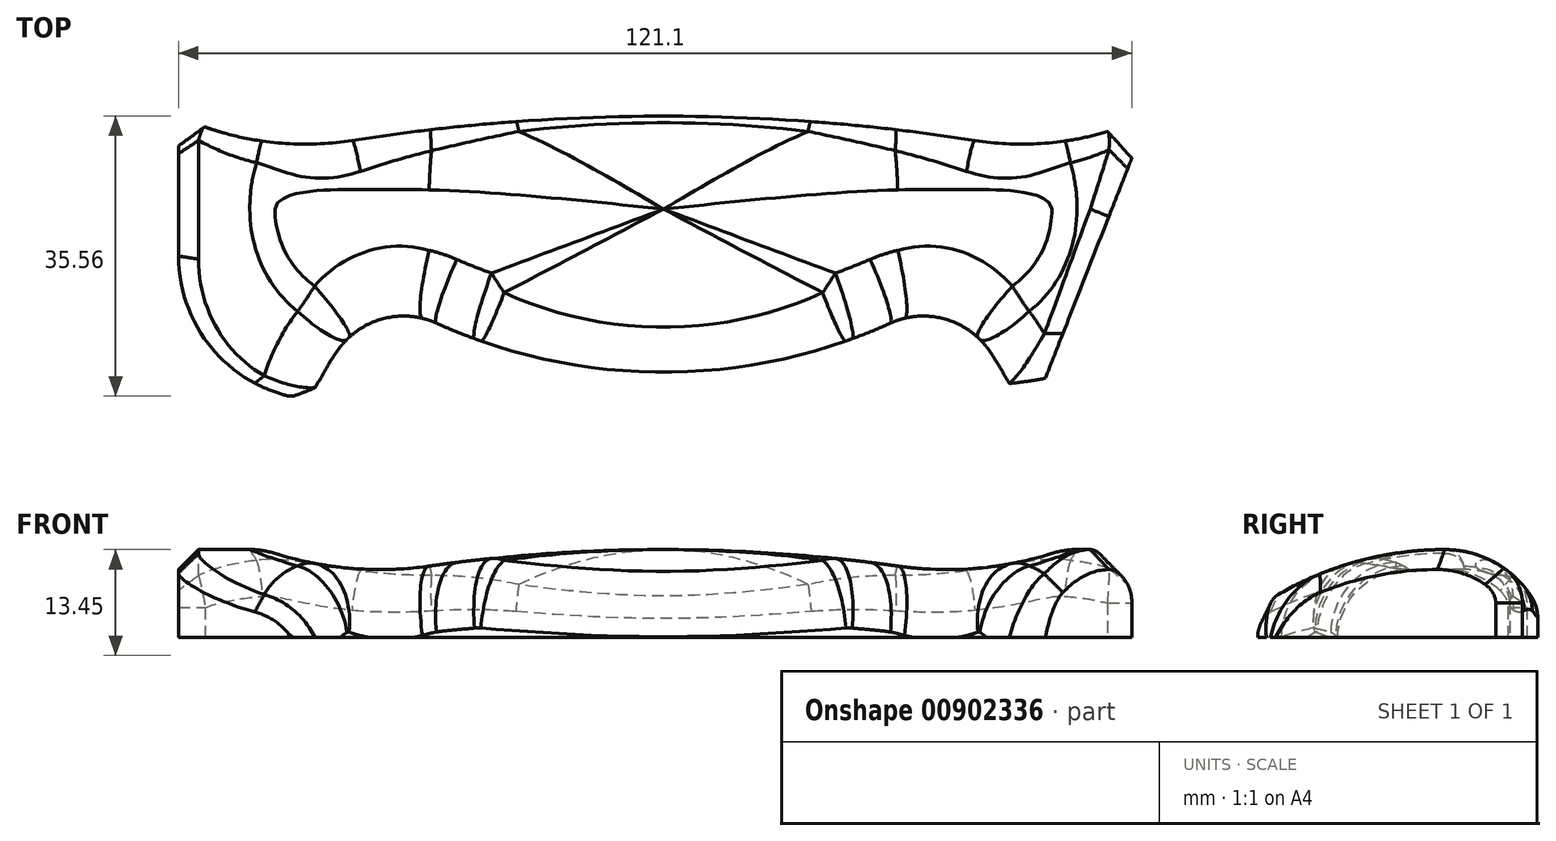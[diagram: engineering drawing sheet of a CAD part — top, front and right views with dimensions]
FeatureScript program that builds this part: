
annotation { "Feature Type Name" : "Feature", "Feature Type Description" : "" }
export const myFeature = defineFeature(function(context is Context, id is Id, definition is map)
    precondition{}
    {
        {
            var Q0;
            Q0=qCreatedBy(makeId("Top.planeOp"),FACE);
            var sketch = newSketch(context, id + "F0", { "sketchPlane" : qUnion([Q0])});
            skLineSegment(sketch, "E0", {"start": v(-61.6, 35.56) * mm, "end": v(-47.63, 0) * mm, "construction": true});
            skLineSegment(sketch, "E1", {"start": v(-47.62, 0) * mm, "end": v(47.62, 0) * mm, "construction": true});
            skLineSegment(sketch, "E2", {"start": v(47.63, 0) * mm, "end": v(61.6, 35.56) * mm, "construction": true});
            skLineSegment(sketch, "E3", {"start": v(61.6, 35.56) * mm, "end": v(-61.6, 35.56) * mm, "construction": true});
            skLineSegment(sketch, "E4", {"start": v(0, 0) * mm, "end": v(0, 35.56) * mm, "construction": true});
            skSolve(sketch);
        }
        {
            var Q0;
            Q0=qCreatedBy(makeId("Top.planeOp"),FACE);
            var sketch = newSketch(context, id + "F1", { "sketchPlane" : qUnion([Q0])});
            skLineSegment(sketch, "E5.0", {"start": v(61.6, 35.56) * mm, "end": v(-61.6, 35.56) * mm, "construction": true});
            skLineSegment(sketch, "E6.0", {"start": v(-61.6, 35.56) * mm, "end": v(-47.63, 0) * mm, "construction": true});
            skLineSegment(sketch, "E7.0", {"start": v(-47.62, 0) * mm, "end": v(47.62, 0) * mm, "construction": true});
            skLineSegment(sketch, "E8.0", {"start": v(47.63, 0) * mm, "end": v(61.6, 35.56) * mm, "construction": true});
            skArc(sketch, "E9", {"start": v(58.88, 28.64) * mm, "mid": v(49.26, 30.74) * mm, "end": v(39.57, 32.46) * mm, "construction": true});
            skArc(sketch, "E10", {"start": v(39.57, 32.46) * mm, "mid": v(50.81, 32.37) * mm, "end": v(61.6, 35.56) * mm});
            skArc(sketch, "E11", {"start": v(-28.83, 9.25) * mm, "mid": v(-38.53, 8.54) * mm, "end": v(-43.18, 0) * mm});
            skArc(sketch, "E12", {"start": v(-28.83, 9.25) * mm, "mid": v(0, 3.03) * mm, "end": v(28.83, 9.25) * mm});
            skArc(sketch, "E13", {"start": v(39.57, 32.46) * mm, "mid": v(0, 35.56) * mm, "end": v(-39.57, 32.46) * mm});
            skLineSegment(sketch, "E14", {"start": v(61.6, 35.56) * mm, "end": v(47.63, 0) * mm});
            skLineSegment(sketch, "E15", {"start": v(43.18, 0) * mm, "end": v(47.62, 0) * mm});
            skArc(sketch, "E16", {"start": v(43.18, 0) * mm, "mid": v(38.53, 8.54) * mm, "end": v(28.83, 9.25) * mm});
            skLineSegment(sketch, "E17", {"start": v(-47.63, 0) * mm, "end": v(-43.18, 0) * mm});
            skLineSegment(sketch, "E18", {"start": v(0, -218.44) * mm, "end": v(0, 72.88) * mm, "construction": true});
            skArc(sketch, "E19", {"start": v(-61.6, 35.56) * mm, "mid": v(-50.81, 32.37) * mm, "end": v(-39.57, 32.46) * mm});
            skArc(sketch, "E20", {"start": v(-39.57, 32.46) * mm, "mid": v(-49.26, 30.74) * mm, "end": v(-58.88, 28.64) * mm, "construction": true});
            skLineSegment(sketch, "E21", {"start": v(-61.6, 35.56) * mm, "end": v(-61.6, 17.78) * mm});
            skLineSegment(sketch, "E22", {"start": v(-61.6, 17.78) * mm, "end": v(-54.61, 17.78) * mm, "construction": true});
            skArc(sketch, "E23", {"start": v(-61.6, 17.78) * mm, "mid": v(-57.68, 6.47) * mm, "end": v(-47.63, 0) * mm});
            skSolve(sketch);
        }
        {
            var Q0;
            Q0=qSketchRegion(id+"F1",true);
            extrude(context, id + "F2", {"entities" : qUnion([Q0]), "depth" : 19.05 * mm, "offsetDistance" : 25.4 * mm});
        }
        {
            var Q0;
            Q0=qCreatedBy(makeId("Right.planeOp"),FACE);
            var sketch = newSketch(context, id + "F3", { "sketchPlane" : qUnion([Q0])});
            skLineSegment(sketch, "E24.0", {"start": v(35.56, 0) * mm, "end": v(0, 0) * mm, "construction": true});
            skLineSegment(sketch, "E25", {"start": v(35.56, 0) * mm, "end": v(35.56, 3.8) * mm, "construction": true});
            skLineSegment(sketch, "E26", {"start": v(35.56, 3.8) * mm, "end": v(35.56, 3.8) * mm});
            skLineSegment(sketch, "E27", {"start": v(0, 3.8) * mm, "end": v(0, 0) * mm, "construction": true});
            skLineSegment(sketch, "E28", {"start": v(23.75, 19.05) * mm, "end": v(23.75, -1.98) * mm, "construction": true});
            skArc(sketch, "E29", {"start": v(23.75, 11.18) * mm, "mid": v(11.32, 9.3) * mm, "end": v(0, 3.8) * mm});
            skArc(sketch, "E30", {"start": v(0, 3.8) * mm, "mid": v(36.18, -70.88) * mm, "end": v(23.75, 11.18) * mm, "construction": true});
            skLineSegment(sketch, "E31", {"start": v(35.56, 3.8) * mm, "end": v(0, 3.8) * mm, "construction": true});
            skArc(sketch, "E32", {"start": v(23.75, 11.18) * mm, "mid": v(16.79, -13.14) * mm, "end": v(35.56, 3.81) * mm, "construction": true});
            skArc(sketch, "E33", {"start": v(35.56, 3.81) * mm, "mid": v(30.7, 9.18) * mm, "end": v(23.75, 11.18) * mm});
            skLineSegment(sketch, "E34.0", {"start": v(35.56, 19.05) * mm, "end": v(0, 19.05) * mm});
            skLineSegment(sketch, "E35", {"start": v(35.56, 3.8) * mm, "end": v(35.56, 19.05) * mm});
            skLineSegment(sketch, "E36", {"start": v(0, 19.05) * mm, "end": v(0, 3.8) * mm});
            skSolve(sketch);
        }
        {
            var Q0;
            Q0=qSketchRegion(id+"F3",true);
            extrude(context, id + "F4", {"entities" : qUnion([Q0]), "operationType" : NewBodyOperationType.REMOVE, "endBound" : BoundingType.SYMMETRIC, "depth" : 254 * mm, "offsetDistance" : 25.4 * mm});
        }
        {
            var Q0;
            Q0=qCreatedBy(makeId("Front.planeOp"),FACE);
            var sketch = newSketch(context, id + "F5", { "sketchPlane" : qUnion([Q0])});
            skLineSegment(sketch, "E37.0", {"start": v(-28.83, 0) * mm, "end": v(-43.18, 0) * mm, "construction": true});
            skLineSegment(sketch, "E38.0", {"start": v(43.18, 0) * mm, "end": v(28.83, 0) * mm, "construction": true});
            skLineSegment(sketch, "E39", {"start": v(-36, 53.09) * mm, "end": v(-36, 0) * mm, "construction": true});
            skLineSegment(sketch, "E40", {"start": v(36, 0) * mm, "end": v(36, 53.09) * mm, "construction": true});
            skArc(sketch, "E41", {"start": v(29.76, 9.08) * mm, "mid": v(0, 11.18) * mm, "end": v(-29.76, 9.08) * mm});
            skArc(sketch, "E42", {"start": v(-29.76, 9.08) * mm, "mid": v(0, -412.8) * mm, "end": v(29.76, 9.08) * mm, "construction": true});
            skLineSegment(sketch, "E43", {"start": v(50.81, 11.18) * mm, "end": v(-50.81, 11.18) * mm});
            skArc(sketch, "E44", {"start": v(-50.81, 11.18) * mm, "mid": v(-40.42, 8.86) * mm, "end": v(-29.76, 9.08) * mm});
            skArc(sketch, "E45", {"start": v(-29.76, 9.08) * mm, "mid": v(-31.6, 97.32) * mm, "end": v(-50.81, 11.18) * mm, "construction": true});
            skArc(sketch, "E46", {"start": v(50.81, 11.18) * mm, "mid": v(31.6, 97.32) * mm, "end": v(29.76, 9.08) * mm, "construction": true});
            skArc(sketch, "E47", {"start": v(29.76, 9.08) * mm, "mid": v(40.42, 8.86) * mm, "end": v(50.81, 11.18) * mm});
            skPoint(sketch, "E48.orphan", {"position": v(56.95, 11.18) * mm});
            skLineSegment(sketch, "E49", {"start": v(-36, 11.18) * mm, "end": v(-36, 8.64) * mm, "construction": true});
            skSolve(sketch);
        }
        {
            var Q0;
            Q0=qSketchRegion(id+"F5",true);
            extrude(context, id + "F6", {"entities" : qUnion([Q0]), "operationType" : NewBodyOperationType.REMOVE, "endBound" : BoundingType.THROUGH_ALL, "oppositeDirection" : true, "depth" : 101.6 * mm, "offsetDistance" : 25.4 * mm});
        }
        {
            var Q0;
            {var subQ0=sQuery(id+"F5.wireOp",EDGE,"E41");Q0=makeQuery(id+"F6.boolean.opBoolean","INTERSECT",EDGE,{"derivedFrom":[makeQuery(id+"F4.boolean.opBoolean","COPY",FACE,{"derivedFrom":makeQuery(id+"F4.opExtrude","SWEPT_FACE",FACE,{"disambiguationData":[OSD([sQuery(id+"F3.wireOp",EDGE,"E33")])]})}),makeQuery(id+"F6.opExtrude","SWEPT_FACE",FACE,{"disambiguationData":[OSD([subQ0]),TDD([makeQuery(id+"F5.imprint","IMPRINT",EDGE,{"disambiguationData":[TD([[makeQuery(id+"F5.imprint","INTERSECT",VERTEX,{"derivedFrom":[subQ0,sQuery(id+"F5.wireOp",EDGE,"E44")]}),1.0]])],"derivedFrom":subQ0})])]})]});}
            var Q1;
            {var subQ0=sQuery(id+"F5.wireOp",EDGE,"E41");Q1=makeQuery(id+"F6.boolean.opBoolean","INTERSECT",EDGE,{"derivedFrom":[makeQuery(id+"F4.boolean.opBoolean","COPY",FACE,{"derivedFrom":makeQuery(id+"F4.opExtrude","SWEPT_FACE",FACE,{"disambiguationData":[OSD([sQuery(id+"F3.wireOp",EDGE,"E33")])]})}),makeQuery(id+"F6.opExtrude","SWEPT_FACE",FACE,{"disambiguationData":[OSD([subQ0]),TDD([makeQuery(id+"F5.imprint","IMPRINT",EDGE,{"disambiguationData":[TD([[makeQuery(id+"F5.imprint","INTERSECT",VERTEX,{"derivedFrom":[subQ0,sQuery(id+"F5.wireOp",EDGE,"E47")]}),-1.0]])],"derivedFrom":subQ0})])]})]});}
            var Q2;
            {var subQ0=sQuery(id+"F5.wireOp",EDGE,"E41");Q2=makeQuery(id+"F6.boolean.opBoolean","INTERSECT",EDGE,{"derivedFrom":[makeQuery(id+"F4.boolean.opBoolean","COPY",FACE,{"derivedFrom":makeQuery(id+"F4.opExtrude","SWEPT_FACE",FACE,{"disambiguationData":[OSD([sQuery(id+"F3.wireOp",EDGE,"E29")])]})}),makeQuery(id+"F6.opExtrude","SWEPT_FACE",FACE,{"disambiguationData":[OSD([subQ0]),TDD([makeQuery(id+"F5.imprint","IMPRINT",EDGE,{"disambiguationData":[TD([[makeQuery(id+"F5.imprint","INTERSECT",VERTEX,{"derivedFrom":[subQ0,sQuery(id+"F5.wireOp",EDGE,"E47")]}),-1.0]])],"derivedFrom":subQ0})])]})]});}
            var Q3;
            {var subQ0=sQuery(id+"F5.wireOp",EDGE,"E41");Q3=makeQuery(id+"F6.boolean.opBoolean","INTERSECT",EDGE,{"derivedFrom":[makeQuery(id+"F4.boolean.opBoolean","COPY",FACE,{"derivedFrom":makeQuery(id+"F4.opExtrude","SWEPT_FACE",FACE,{"disambiguationData":[OSD([sQuery(id+"F3.wireOp",EDGE,"E29")])]})}),makeQuery(id+"F6.opExtrude","SWEPT_FACE",FACE,{"disambiguationData":[OSD([subQ0]),TDD([makeQuery(id+"F5.imprint","IMPRINT",EDGE,{"disambiguationData":[TD([[makeQuery(id+"F5.imprint","INTERSECT",VERTEX,{"derivedFrom":[subQ0,sQuery(id+"F5.wireOp",EDGE,"E44")]}),1.0]])],"derivedFrom":subQ0})])]})]});}
            fillet(context, id + "F7", {"entities" : qUnion([Q0, Q1, Q2, Q3]), "radius" : 10.67 * mm, "tangentPropagation" : true, "allowEdgeOverflow" : false});
        }
        {
            var Q0;
            Q0=makeQuery(id+"F4.boolean.opBoolean","INTERSECT",EDGE,{"derivedFrom":[makeQuery(id+"F2.opExtrude","SWEPT_FACE",FACE,{"disambiguationData":[OSD([sQuery(id+"F1.wireOp",EDGE,"E13")])]}),makeQuery(id+"F4.opExtrude","SWEPT_FACE",FACE,{"disambiguationData":[OSD([sQuery(id+"F3.wireOp",EDGE,"E33")])]})]});
            fillet(context, id + "F8", {"entities" : qUnion([Q0]), "radius" : 5.08 * mm, "tangentPropagation" : true, "allowEdgeOverflow" : false});
        }
        {
            var Q0;
            Q0=makeQuery(id+"F4.boolean.opBoolean","INTERSECT",EDGE,{"derivedFrom":[makeQuery(id+"F2.opExtrude","SWEPT_FACE",FACE,{"disambiguationData":[OSD([sQuery(id+"F1.wireOp",EDGE,"E12")])]}),makeQuery(id+"F4.opExtrude","SWEPT_FACE",FACE,{"disambiguationData":[OSD([sQuery(id+"F3.wireOp",EDGE,"E29")])]})]});
            fillet(context, id + "F9", {"entities" : qUnion([Q0]), "radius" : 8.9 * mm, "tangentPropagation" : true, "allowEdgeOverflow" : false});
        }
        {
            var Q0;
            Q0=makeQuery(id+"F4.boolean.opBoolean","INTERSECT",EDGE,{"derivedFrom":[makeQuery(id+"F2.opExtrude","SWEPT_FACE",FACE,{"disambiguationData":[OSD([sQuery(id+"F1.wireOp",EDGE,"E14")])]}),makeQuery(id+"F4.opExtrude","SWEPT_FACE",FACE,{"disambiguationData":[OSD([sQuery(id+"F3.wireOp",EDGE,"E33")])]})]});
            var Q1;
            Q1=makeQuery(id+"F4.boolean.opBoolean","INTERSECT",EDGE,{"derivedFrom":[makeQuery(id+"F2.opExtrude","SWEPT_FACE",FACE,{"disambiguationData":[OSD([sQuery(id+"F1.wireOp",EDGE,"E21")])]}),makeQuery(id+"F4.opExtrude","SWEPT_FACE",FACE,{"disambiguationData":[OSD([sQuery(id+"F3.wireOp",EDGE,"E33")])]})]});
            chamfer(context, id + "F10", {"entities" : qUnion([Q0, Q1]), "width" : 2.54 * mm, "tangentPropagation" : true});
        }
    });
